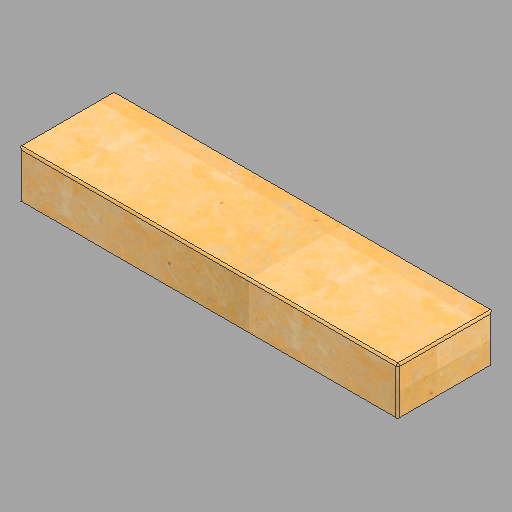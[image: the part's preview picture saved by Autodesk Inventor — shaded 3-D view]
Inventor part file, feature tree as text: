
AUTODESK INVENTOR PART (.ipt)
format: ipt  version: 2023 (Build 270158030, 158C)  size: 267,264 bytes
history: native  units: in
note: dims shown in document units (in); Inventor stores cm internally (conversion verified against a paired STEP export)
features: fillet x4, extrude x1, direct_edit x1, sketch x1, move_body x1
ambient origin geometry x8: Origin, YZ Plane, XZ Plane, XY Plane, X Axis, Y Axis, Z Axis, Center Point
bodies: Solid1 (feature_tree)
feature tree (8):
  extrude  "Extrusion1"  Depth=10.0in
  fillet  "Fillet1"  Radius=48.0in
  fillet  "Fillet2"  Radius=0.25in
  fillet  "Fillet5"  Radius=0.125in
  fillet  "Fillet6"  Radius=0.25in
  direct_edit  "Direct Edit1"
  sketch  "Sketch1"  dims[d0=6.0in d1=10.0in d2=48.0in d3=0.0in d4=0.25in d5=0.125in d12=0.25in d13=0.125in d14=0.0in d15=0.0in d16=2.0in]
  move_body  "Move1"
